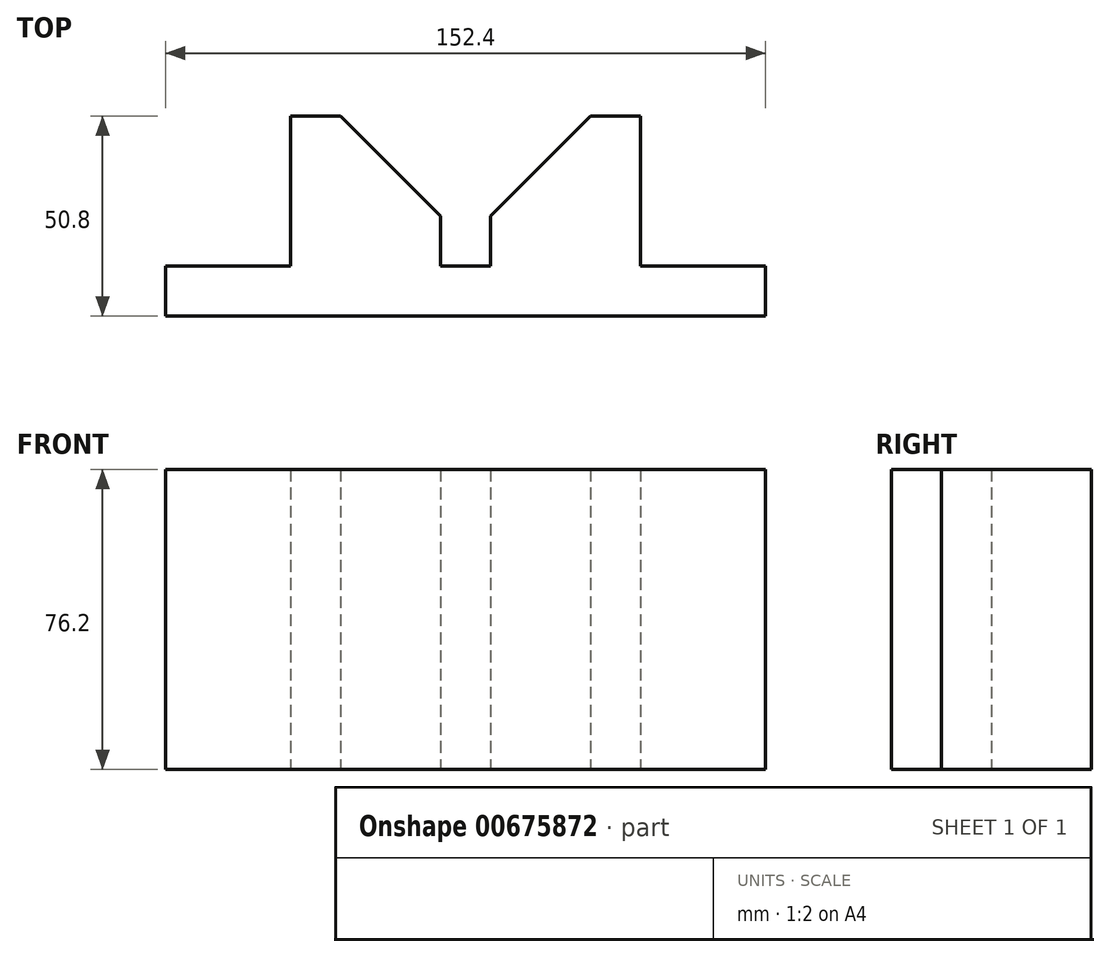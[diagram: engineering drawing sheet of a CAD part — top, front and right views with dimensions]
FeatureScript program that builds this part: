
annotation { "Feature Type Name" : "Feature", "Feature Type Description" : "" }
export const myFeature = defineFeature(function(context is Context, id is Id, definition is map)
    precondition{}
    {
        {
            var Q0;
            Q0=qCreatedBy(makeId("Top.planeOp"),FACE);
            var sketch = newSketch(context, id + "F0", { "sketchPlane" : qUnion([Q0])});
            skLineSegment(sketch, "E0", {"start": v(-70.96, 35.9) * mm, "end": v(-70.96, -2.2) * mm});
            skLineSegment(sketch, "E1", {"start": v(-70.96, -2.2) * mm, "end": v(-102.7, -2.2) * mm});
            skLineSegment(sketch, "E2", {"start": v(-102.7, -2.2) * mm, "end": v(-102.7, -14.9) * mm});
            skLineSegment(sketch, "E3", {"start": v(-102.7, -14.9) * mm, "end": v(49.7, -14.9) * mm});
            skLineSegment(sketch, "E4", {"start": v(49.7, -14.9) * mm, "end": v(49.7, -2.2) * mm});
            skLineSegment(sketch, "E5", {"start": v(49.7, -2.2) * mm, "end": v(17.94, -2.2) * mm});
            skLineSegment(sketch, "E6", {"start": v(17.94, -2.2) * mm, "end": v(17.94, 35.9) * mm});
            skLineSegment(sketch, "E7", {"start": v(-70.96, 35.9) * mm, "end": v(-58.26, 35.9) * mm});
            skLineSegment(sketch, "E8", {"start": v(5.24, 35.9) * mm, "end": v(17.94, 35.9) * mm});
            skLineSegment(sketch, "E9", {"start": v(-32.86, 10.5) * mm, "end": v(-32.86, -2.2) * mm});
            skLineSegment(sketch, "E10", {"start": v(-32.86, -2.2) * mm, "end": v(-20.16, -2.2) * mm});
            skLineSegment(sketch, "E11", {"start": v(-20.16, 10.5) * mm, "end": v(-20.16, -2.2) * mm});
            skLineSegment(sketch, "E12", {"start": v(-20.16, 10.5) * mm, "end": v(5.24, 35.9) * mm});
            skLineSegment(sketch, "E13", {"start": v(-32.86, 10.5) * mm, "end": v(-58.26, 35.9) * mm});
            skSolve(sketch);
        }
        {
            var Q0;
            Q0 = qSketchRegion(id + "F0", true);
            extrude(context, id + "F1", {"entities" : qUnion([Q0]), "depth" : 76.2 * mm, "offsetDistance" : 25.4 * mm});
        }
    });
